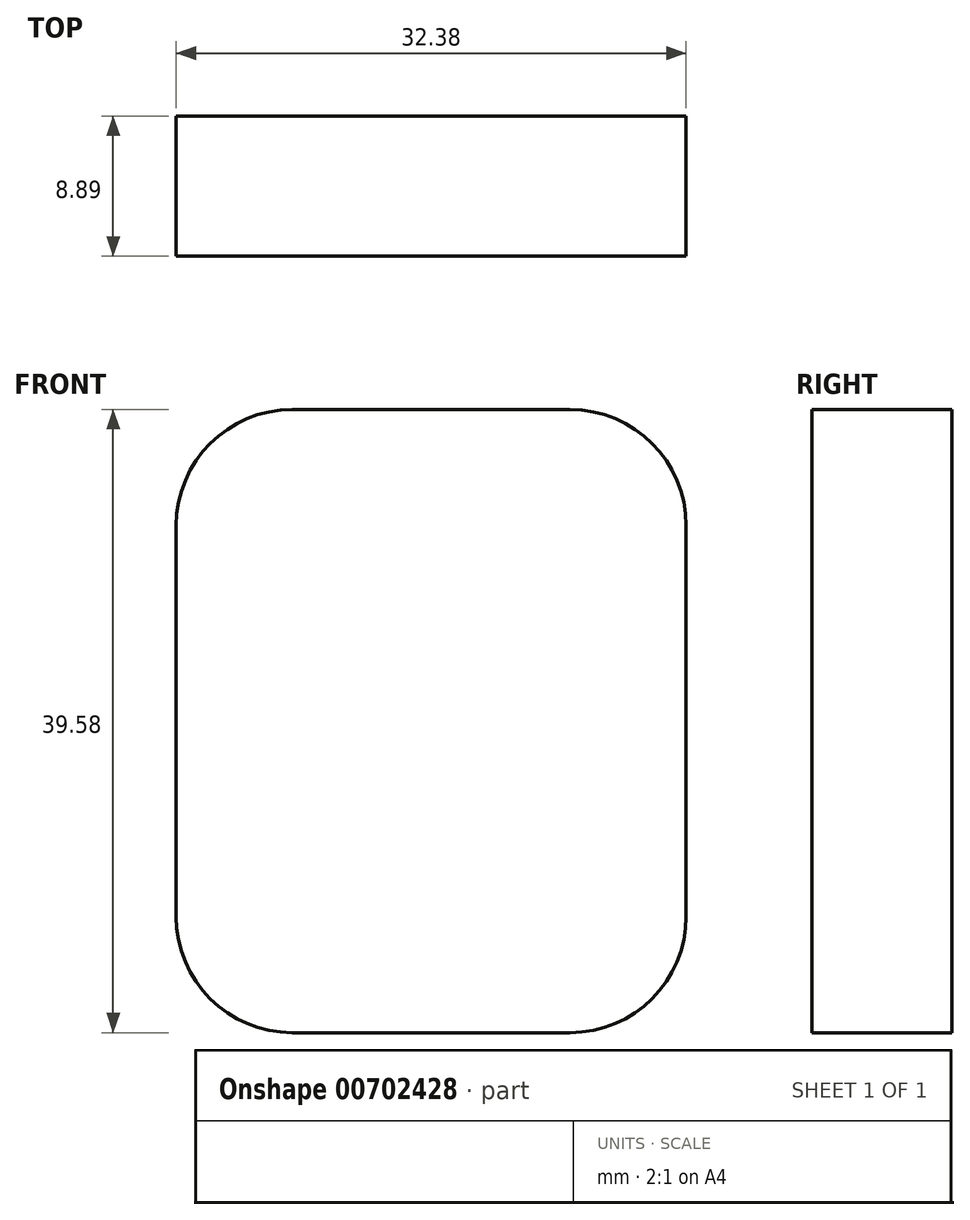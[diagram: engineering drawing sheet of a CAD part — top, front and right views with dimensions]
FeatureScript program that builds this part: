
annotation { "Feature Type Name" : "Feature", "Feature Type Description" : "" }
export const myFeature = defineFeature(function(context is Context, id is Id, definition is map)
    precondition{}
    {
        {
            var Q0;
            Q0=qCreatedBy(makeId("Front.planeOp"),FACE);
            var sketch = newSketch(context, id + "F0", { "sketchPlane" : qUnion([Q0])});
            skLineSegment(sketch, "E0.bottom", {"start": v(8.83, -19.8) * mm, "end": v(-8.83, -19.8) * mm});
            skLineSegment(sketch, "E0.top", {"start": v(8.83, 19.8) * mm, "end": v(-8.83, 19.8) * mm});
            skLineSegment(sketch, "E0.left", {"start": v(16.2, -12.42) * mm, "end": v(16.2, 12.42) * mm});
            skLineSegment(sketch, "E0.right", {"start": v(-16.2, -12.42) * mm, "end": v(-16.2, 12.42) * mm});
            skPoint(sketch, "E0.middle", {"position": v(0, 0) * mm});
            skPoint(sketch, "E1.visualSharp", {"position": v(-16.2, 19.8) * mm});
            skArc(sketch, "E1.filletArc", {"start": v(-8.83, 19.8) * mm, "mid": v(-14.03, 17.63) * mm, "end": v(-16.2, 12.42) * mm});
            skPoint(sketch, "E2.visualSharp", {"position": v(16.2, 19.8) * mm});
            skArc(sketch, "E2.filletArc", {"start": v(16.2, 12.42) * mm, "mid": v(14.03, 17.63) * mm, "end": v(8.83, 19.8) * mm});
            skPoint(sketch, "E3.visualSharp", {"position": v(-16.2, -19.8) * mm});
            skArc(sketch, "E3.filletArc", {"start": v(-16.2, -12.42) * mm, "mid": v(-14.03, -17.63) * mm, "end": v(-8.83, -19.8) * mm});
            skPoint(sketch, "E4.visualSharp", {"position": v(16.2, -19.8) * mm});
            skArc(sketch, "E4.filletArc", {"start": v(8.83, -19.8) * mm, "mid": v(14.03, -17.63) * mm, "end": v(16.2, -12.42) * mm});
            skSolve(sketch);
        }
        {
            var Q0;
            Q0 = qSketchRegion(id + "F0", true);
            extrude(context, id + "F1", {"entities" : qUnion([Q0]), "depth" : 8.9 * mm, "offsetDistance" : 25.4 * mm});
        }
    });
